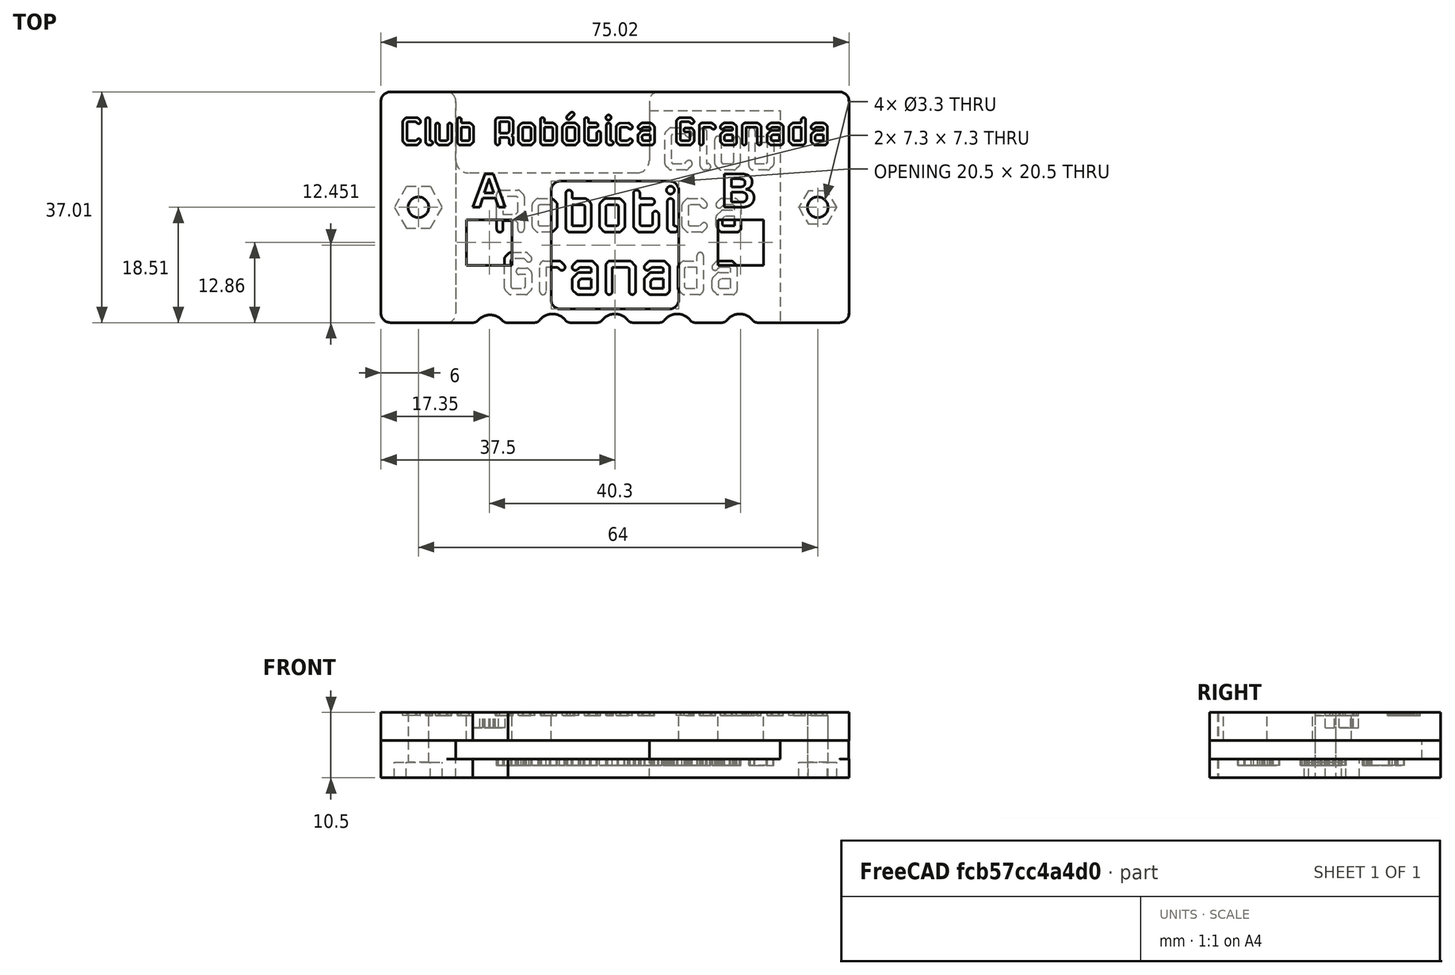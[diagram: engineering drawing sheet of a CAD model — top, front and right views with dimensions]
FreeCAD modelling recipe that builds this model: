
FCSTD DOCUMENT  (FreeCAD 0.18.4R)
Label: proteccion
License: All rights reserved
LicenseURL: http://en.wikipedia.org/wiki/All_rights_reserved
objects: Sketcher::SketchObject×8, PartDesign::Pad×8, PartDesign::Body×8, Part::Part2DObjectPython×6, Part::Extrusion×6, Part::MultiFuse×5, Part::Cut×4, Mesh::Feature×2
note: 53 computed .brp shape members not serialized (recipe doc carries the construction recipe); baked Part::Feature solids carry a one-line shape summary decoded from their .brp

FEATURE [Mesh::Feature] bas_sans_nom  label="basevv"
  Placement = pos=(0,0,0) rot=(1,0,0;1.5708rad)
FEATURE [Mesh::Feature] Haut_sans_nom  label="tapavv"
  Placement = pos=(0,0,0) rot=(1,0,0;1.5708rad)
FEATURE [Sketcher::SketchObject] Sketch
  MapMode = 5
  Support = -> [XY_Plane]
  sketch-geometry (59):
    g0: LineSegment [constr] StartX=-32.5 StartY=18.5 StartZ=0 EndX=32.5 EndY=18.5 EndZ=0
    g1: LineSegment [constr] StartX=32.5 StartY=18.5 StartZ=0 EndX=32.5 EndY=-18.5 EndZ=0
    g2: LineSegment [constr] StartX=32.5 StartY=-18.5 StartZ=0 EndX=-32.5 EndY=-18.5 EndZ=0
    g3: LineSegment [constr] StartX=-32.5 StartY=-18.5 StartZ=0 EndX=-32.5 EndY=18.5 EndZ=0
    g4: LineSegment StartX=-31 StartY=18.5 StartZ=0 EndX=-27 EndY=18.5 EndZ=0
    g5: LineSegment [constr] StartX=32.5 StartY=17 StartZ=0 EndX=32.5 EndY=-17 EndZ=0
    g6: LineSegment StartX=31 StartY=-18.5 StartZ=0 EndX=22.8496 EndY=-18.5 EndZ=0
    g7: LineSegment [constr] StartX=-32.5 StartY=-17 StartZ=0 EndX=-32.5 EndY=17 EndZ=0
    g8: ArcOfCircle [constr] CenterX=-31 CenterY=17 CenterZ=0 NormalX=0 NormalY=0 NormalZ=1 AngleXU=0 Radius=1.5 StartAngle=1.5708 EndAngle=3.14159
    g9: ArcOfCircle [constr] CenterX=-31 CenterY=-17 CenterZ=0 NormalX=0 NormalY=0 NormalZ=1 AngleXU=0 Radius=1.5 StartAngle=3.14159 EndAngle=4.71239
    g10: ArcOfCircle [constr] CenterX=31 CenterY=17 CenterZ=0 NormalX=0 NormalY=0 NormalZ=1 AngleXU=0 Radius=1.5 StartAngle=-9e-16 EndAngle=1.5708
    g11: ArcOfCircle [constr] CenterX=31 CenterY=-17 CenterZ=0 NormalX=0 NormalY=0 NormalZ=1 AngleXU=0 Radius=1.5 StartAngle=4.71239 EndAngle=6.28319
    g12: LineSegment StartX=5.5 StartY=17 StartZ=0 EndX=5.5 EndY=7.5 EndZ=0
    g13: LineSegment StartX=3.5 StartY=5.5 StartZ=0 EndX=-23.5 EndY=5.5 EndZ=0
    g14: LineSegment StartX=-25.5 StartY=7.5 StartZ=0 EndX=-25.5 EndY=17 EndZ=0
    g15: LineSegment StartX=7 StartY=18.5 StartZ=0 EndX=31 EndY=18.5 EndZ=0
    g16: ArcOfCircle CenterX=-27 CenterY=17 CenterZ=0 NormalX=0 NormalY=0 NormalZ=1 AngleXU=0 Radius=1.5 StartAngle=1e-16 EndAngle=1.5708
    g17: ArcOfCircle CenterX=7 CenterY=17 CenterZ=0 NormalX=0 NormalY=0 NormalZ=1 AngleXU=0 Radius=1.5 StartAngle=1.5708 EndAngle=3.14159
    g18: ArcOfCircle CenterX=-23.5 CenterY=7.5 CenterZ=0 NormalX=0 NormalY=0 NormalZ=1 AngleXU=0 Radius=2 StartAngle=3.14159 EndAngle=4.71239
    g19: ArcOfCircle CenterX=3.5 CenterY=7.5 CenterZ=0 NormalX=0 NormalY=0 NormalZ=1 AngleXU=0 Radius=2 StartAngle=4.71239 EndAngle=6.28319
    g20: LineSegment [constr] StartX=-20 StartY=-19.7 StartZ=0 EndX=27.6448 EndY=-19.7 EndZ=0
    g21: LineSegment [constr] StartX=-10 StartY=-19.7 StartZ=0 EndX=-10 EndY=-21.3595 EndZ=0
    g22: LineSegment [constr] StartX=-15 StartY=-19.7 StartZ=0 EndX=-15 EndY=-20.3977 EndZ=0
    g23: LineSegment [constr] StartX=-5 StartY=-19.7 StartZ=0 EndX=-5 EndY=-20.6594 EndZ=0
    g24: LineSegment [constr] StartX=0 StartY=-19.7 StartZ=0 EndX=0 EndY=-21.7167 EndZ=0
    g25: LineSegment [constr] StartX=5 StartY=-19.7 StartZ=0 EndX=5 EndY=-20.9237 EndZ=0
    g26: LineSegment [constr] StartX=10 StartY=-19.7 StartZ=0 EndX=10 EndY=-20.8482 EndZ=0
    g27: LineSegment [constr] StartX=15 StartY=-19.7 StartZ=0 EndX=15 EndY=-20.886 EndZ=0
    g28: LineSegment [constr] StartX=20 StartY=-19.7 StartZ=0 EndX=20 EndY=-21.4524 EndZ=0
    g29: ArcOfCircle CenterX=-2.84955 CenterY=-17.5 CenterZ=0 NormalX=0 NormalY=0 NormalZ=1 AngleXU=0 Radius=1 StartAngle=4.71239 EndAngle=5.62572
    g30: ArcOfCircle CenterX=0 CenterY=-19.7 CenterZ=0 NormalX=0 NormalY=0 NormalZ=1 AngleXU=0 Radius=2.6 StartAngle=0.657467 EndAngle=2.48413
    g31: ArcOfCircle CenterX=2.84955 CenterY=-17.5 CenterZ=0 NormalX=0 NormalY=0 NormalZ=1 AngleXU=0 Radius=1 StartAngle=3.79906 EndAngle=4.71232
    g32: LineSegment StartX=-2.84955 StartY=-18.5 StartZ=0 EndX=-7.15054 EndY=-18.5 EndZ=0
    g33: ArcOfCircle CenterX=7.15045 CenterY=-17.5 CenterZ=0 NormalX=0 NormalY=0 NormalZ=1 AngleXU=0 Radius=1 StartAngle=4.71239 EndAngle=5.62572
    g34: ArcOfCircle CenterX=10 CenterY=-19.7 CenterZ=0 NormalX=0 NormalY=0 NormalZ=1 AngleXU=0 Radius=2.6 StartAngle=0.657467 EndAngle=2.48413
    g35: ArcOfCircle CenterX=12.8496 CenterY=-17.5 CenterZ=0 NormalX=0 NormalY=0 NormalZ=1 AngleXU=0 Radius=1 StartAngle=3.79906 EndAngle=4.71239
    g36: LineSegment StartX=7.15045 StartY=-18.5 StartZ=0 EndX=2.84948 EndY=-18.5 EndZ=0
    g37: ArcOfCircle CenterX=17.1504 CenterY=-17.5 CenterZ=0 NormalX=0 NormalY=0 NormalZ=1 AngleXU=0 Radius=1 StartAngle=4.71239 EndAngle=5.62572
    g38: ArcOfCircle CenterX=20 CenterY=-19.7 CenterZ=0 NormalX=0 NormalY=0 NormalZ=1 AngleXU=0 Radius=2.6 StartAngle=0.657467 EndAngle=2.48413
    g39: ArcOfCircle CenterX=22.8496 CenterY=-17.5 CenterZ=0 NormalX=0 NormalY=0 NormalZ=1 AngleXU=0 Radius=1 StartAngle=3.79906 EndAngle=4.71239
    g40: LineSegment StartX=17.1504 StartY=-18.5 StartZ=0 EndX=12.8496 EndY=-18.5 EndZ=0
    g41: ArcOfCircle CenterX=-7.15046 CenterY=-17.5 CenterZ=0 NormalX=0 NormalY=0 NormalZ=1 AngleXU=0 Radius=1 StartAngle=3.79906 EndAngle=4.71232
    g42: ArcOfCircle CenterX=-10 CenterY=-19.7 CenterZ=0 NormalX=0 NormalY=0 NormalZ=1 AngleXU=0 Radius=2.6 StartAngle=0.65747 EndAngle=2.48412
    g43: ArcOfCircle CenterX=-12.8496 CenterY=-17.5 CenterZ=0 NormalX=0 NormalY=0 NormalZ=1 AngleXU=0 Radius=1 StartAngle=4.71239 EndAngle=5.62572
    g44: ArcOfCircle CenterX=-17.2845 CenterY=-17.511 CenterZ=0 NormalX=0 NormalY=0 NormalZ=1 AngleXU=0 Radius=1 StartAngle=3.8529 EndAngle=4.86087
    g45: ArcOfCircle CenterX=-20.0115 CenterY=-19.8612 CenterZ=0 NormalX=0 NormalY=0 NormalZ=1 AngleXU=0 Radius=2.6 StartAngle=0.71131 EndAngle=2.42648
    g46: ArcOfCircle CenterX=-22.7296 CenterY=-17.5006 CenterZ=0 NormalX=0 NormalY=0 NormalZ=1 AngleXU=0 Radius=1 StartAngle=4.67644 EndAngle=5.56807
    g47: LineSegment StartX=-17.1366 StartY=-18.5 StartZ=0 EndX=-12.8496 EndY=-18.5 EndZ=0
    g48: LineSegment StartX=-31 StartY=-18.5 StartZ=0 EndX=-22.7656 EndY=-18.5 EndZ=0
    g49: LineSegment StartX=-31 StartY=18.5 StartZ=0 EndX=-36 EndY=18.5 EndZ=0
    g50: LineSegment StartX=-37.5 StartY=17 StartZ=0 EndX=-37.5 EndY=-17 EndZ=0
    g51: LineSegment StartX=-36 StartY=-18.5 StartZ=0 EndX=-31 EndY=-18.5 EndZ=0
    g52: ArcOfCircle CenterX=-36 CenterY=17 CenterZ=0 NormalX=0 NormalY=0 NormalZ=1 AngleXU=0 Radius=1.5 StartAngle=1.5708 EndAngle=3.14159
    g53: ArcOfCircle CenterX=-36 CenterY=-17 CenterZ=0 NormalX=0 NormalY=0 NormalZ=1 AngleXU=0 Radius=1.5 StartAngle=3.14159 EndAngle=4.71239
    g54: LineSegment StartX=31 StartY=18.5 StartZ=0 EndX=36.0154 EndY=18.5 EndZ=0
    g55: LineSegment StartX=37.5154 StartY=17 StartZ=0 EndX=37.5154 EndY=-17 EndZ=0
    g56: LineSegment StartX=36.0154 StartY=-18.5 StartZ=0 EndX=31 EndY=-18.5 EndZ=0
    g57: ArcOfCircle CenterX=36.0154 CenterY=17 CenterZ=0 NormalX=0 NormalY=0 NormalZ=1 AngleXU=0 Radius=1.5 StartAngle=-9e-16 EndAngle=1.5708
    g58: ArcOfCircle CenterX=36.0154 CenterY=-17 CenterZ=0 NormalX=0 NormalY=0 NormalZ=1 AngleXU=0 Radius=1.5 StartAngle=4.71239 EndAngle=6.28319
  constraints (143):
    c: Coincident(g0,g1)
    c: Coincident(g1,g2)
    c: Coincident(g2,g3)
    c: Coincident(g3,g0)
    c: Horizontal(g0)
    c: Horizontal(g2)
    c: Vertical(g1)
    c: Vertical(g3)
    c: DistanceY(g1,g1) = 37
    c: Symmetric(g0,g1,g-1)
    c: Horizontal(g4)
    c: Horizontal(g6)
    c: Vertical(g5)
    c: Vertical(g7)
    c: Tangent(g4,g8) = 1.5708
    c: Tangent(g7,g8) = 1.5708
    c: Tangent(g7,g9) = 1.5708
    c: Coincident(g15,g10) = 1.5708
    c: Tangent(g5,g10) = 1.5708
    c: Tangent(g6,g11) = 1.5708
    c: Tangent(g5,g11) = 1.5708
    c: Equal(g8,g10)
    c: Equal(g10,g11)
    c: Equal(g11,g9)
    c: Radius(g8) = 1.5
    c: PointOnObject(g5,g1)
    c: PointOnObject(g15,g0)
    c: Horizontal(g13)
    c: Vertical(g12)
    c: Vertical(g14)
    c: Tangent(g4,g15)
    c: Tangent(g4,g16) = 1.5708
    c: Tangent(g14,g16) = -1.5708
    c: Tangent(g15,g17) = 1.5708
    c: Tangent(g12,g17) = -1.5708
    c: Equal(g8,g16)
    c: Equal(g16,g17)
    c: Tangent(g14,g18) = 1.5708
    c: Tangent(g13,g18) = 1.5708
    c: Tangent(g13,g19) = 1.5708
    c: Tangent(g12,g19) = 1.5708
    c: Equal(g19,g18)
    c: Radius(g18) = 2
    c: DistanceY(g13,g15) = 13
    c: DistanceX(g14,g12) = 31
    c: DistanceX(g7,g14) = 7
    c: Horizontal(g20)
    c: PointOnObject(g21,g20)
    c: Vertical(g21)
    c: PointOnObject(g22,g20)
    c: Vertical(g22)
    c: PointOnObject(g23,g20)
    c: DistanceX(g22,g21) = 5
    c: Vertical(g23)
    c: PointOnObject(g24,g20)
    c: Vertical(g24)
    c: PointOnObject(g25,g20)
    c: Vertical(g25)
    c: PointOnObject(g26,g20)
    c: Vertical(g26)
    c: PointOnObject(g27,g20)
    c: Vertical(g27)
    c: PointOnObject(g28,g20)
    c: Vertical(g28)
    c: PointOnObject(g24,g-2)
    c: DistanceX(g21,g23) = 5
    c: DistanceX(g24,g25) = 5
    c: DistanceX(g25,g26) = 5
    c: DistanceX(g26,g27) = 5
    c: DistanceX(g27,g28) = 5
    c: Tangent(g30,g31) = 1.5708
    c: Tangent(g30,g29) = 1.5708
    c: Radius(g30) = 2.6
    c: Equal(g31,g29)
    c: Radius(g31) = 1
    c: Tangent(g6,g32)
    c: Coincident(g29,g32)
    c: Coincident(g36,g31)
    c: Tangent(g34,g35) = 1.5708
    c: Tangent(g34,g33) = 1.5708
    c: Radius(g34) = 2.6
    c: Equal(g35,g33)
    c: Radius(g35) = 1
    c: Coincident(g26,g34)
    c: Coincident(g40,g35)
    c: Coincident(g36,g33)
    c: Tangent(g6,g36)
    c: Tangent(g38,g39) = 1.5708
    c: Tangent(g38,g37) = 1.5708
    c: Radius(g38) = 2.6
    c: Equal(g39,g37)
    c: Radius(g39) = 1
    c: Tangent(g6,g40)
    c: Coincident(g24,g30)
    c: Coincident(g37,g40)
    c: Coincident(g38,g28)
    c: Coincident(g39,g6)
    c: Tangent(g42,g41) = 1.5708
    c: Tangent(g42,g43) = 1.5708
    c: Radius(g42) = 2.6
    c: Equal(g41,g43)
    c: Radius(g41) = 1
    c: PointOnObject(g43,g2)
    c: Coincident(g32,g41)
    c: Tangent(g45,g44) = 1.5708
    c: Tangent(g45,g46) = 1.5708
    c: Radius(g45) = 2.6
    c: Equal(g44,g46)
    c: Radius(g44) = 1
    c: Coincident(g47,g44)
    c: Coincident(g47,g43)
    c: Horizontal(g47)
    c: Coincident(g48,g9)
    c: Coincident(g48,g46)
    c: Horizontal(g48)
    c: DistanceY(g10,g0) = 1.5
    c: PointOnObject(g9,g2)
    c: DistanceX(g7,g5) = 65
    c: Symmetric(g8,g11,g-1)
    c: Horizontal(g49)
    c: Horizontal(g51)
    c: Vertical(g50)
    c: Coincident(g49,g4)
    c: Coincident(g51,g48)
    c: DistanceX(g2,g48) = 1.5
    c: Tangent(g50,g52) = -1.5708
    c: Tangent(g49,g52) = -1.5708
    c: Equal(g52,g8)
    c: Tangent(g50,g53) = -1.5708
    c: Tangent(g51,g53) = -1.5708
    c: Equal(g9,g53)
    c: DistanceX(g50,g2) = 5
    c: Coincident(g15,g54)
    c: Horizontal(g54)
    c: Vertical(g55)
    c: Coincident(g56,g6)
    c: Horizontal(g56)
    c: Tangent(g54,g57) = 1.5708
    c: Tangent(g55,g57) = 1.5708
    c: Equal(g57,g10)
    c: Tangent(g56,g58) = 1.5708
    c: Tangent(g55,g58) = 1.5708
    c: Equal(g11,g58)
FEATURE [PartDesign::Pad] Pad
  Length = 3
  Length2 = 100
  Profile = -> Sketch
  Refine = true
  Type = 0
FEATURE [PartDesign::Body] Body  label="base"
  Group = -> [Sketch,Pad]
  Origin = -> Origin
  Tip = -> Pad
FEATURE [Part::Part2DObjectPython] ShapeString  # Draft 2D object (typed FeaturePython)
  FontFile = <path>
  Placement = pos=(8,6,2) rot=(0,0,1;0rad)
  Size = 4
  String = Club
  Tracking = 0
FEATURE [Part::Part2DObjectPython] ShapeString001  # Draft 2D object (typed FeaturePython)
  FontFile = <path>
  Placement = pos=(-18.95,-4,2) rot=(0,0,1;0rad)
  Size = 4
  String = Robotica
  Tracking = 0
FEATURE [Part::Part2DObjectPython] ShapeString002  # Draft 2D object (typed FeaturePython)
  FontFile = <path>
  Placement = pos=(-17.7,-14,2) rot=(0,0,1;0rad)
  Size = 4
  String = Granada
  Tracking = 0
FEATURE [Part::Extrusion] Extrude
  Base = -> ShapeString
  Dir = (0,0,1)
  DirMode = 2
  FaceMakerClass = Part::FaceMakerBullseye
  LengthFwd = 10
  LengthRev = 0
  Solid = true
  Symmetric = false
FEATURE [Part::Extrusion] Extrude001
  Base = -> ShapeString001
  Dir = (0,0,1)
  DirMode = 2
  FaceMakerClass = Part::FaceMakerBullseye
  LengthFwd = 10
  LengthRev = 0
  Solid = true
  Symmetric = false
FEATURE [Part::Extrusion] Extrude002
  Base = -> ShapeString002
  Dir = (0,0,1)
  DirMode = 2
  FaceMakerClass = Part::FaceMakerBullseye
  LengthFwd = 10
  LengthRev = 0
  Solid = true
  Symmetric = false
FEATURE [Part::MultiFuse] Fusion
  Refine = true
  Shapes = -> [Extrude,Extrude001,Extrude002]
FEATURE [Sketcher::SketchObject] Sketch004
  MapMode = 5
  Support = -> [XY_Plane001]
  sketch-geometry (16):
    g0: LineSegment [constr] StartX=-32.5 StartY=18.5 StartZ=0 EndX=32.5 EndY=18.5 EndZ=0
    g1: LineSegment [constr] StartX=32.5 StartY=-18.5 StartZ=0 EndX=-32.5 EndY=-18.5 EndZ=0
    g2: LineSegment [constr] StartX=-32.5 StartY=-18.5 StartZ=0 EndX=-32.5 EndY=18.5 EndZ=0
    g3: LineSegment StartX=-31 StartY=18.5 StartZ=0 EndX=-27 EndY=18.5 EndZ=0
    g4: LineSegment [constr] StartX=-32.5 StartY=-17 StartZ=0 EndX=-32.5 EndY=17 EndZ=0
    g5: ArcOfCircle [constr] CenterX=-31 CenterY=17 CenterZ=0 NormalX=0 NormalY=0 NormalZ=1 AngleXU=0 Radius=1.5 StartAngle=1.5708 EndAngle=3.14159
    g6: ArcOfCircle [constr] CenterX=-31 CenterY=-17 CenterZ=0 NormalX=0 NormalY=0 NormalZ=1 AngleXU=0 Radius=1.5 StartAngle=3.14159 EndAngle=4.71239
    g7: LineSegment StartX=-31 StartY=-18.5 StartZ=0 EndX=-27 EndY=-18.5 EndZ=0
    g8: LineSegment StartX=-31 StartY=18.5 StartZ=0 EndX=-36 EndY=18.5 EndZ=0
    g9: LineSegment StartX=-37.5 StartY=17 StartZ=0 EndX=-37.5 EndY=-17 EndZ=0
    g10: LineSegment StartX=-36 StartY=-18.5 StartZ=0 EndX=-31 EndY=-18.5 EndZ=0
    g11: ArcOfCircle CenterX=-36 CenterY=17 CenterZ=0 NormalX=0 NormalY=0 NormalZ=1 AngleXU=0 Radius=1.5 StartAngle=1.5708 EndAngle=3.14159
    g12: ArcOfCircle CenterX=-36 CenterY=-17 CenterZ=0 NormalX=0 NormalY=0 NormalZ=1 AngleXU=0 Radius=1.5 StartAngle=3.14159 EndAngle=4.71239
    g13: LineSegment StartX=-25.5 StartY=17 StartZ=0 EndX=-25.5 EndY=-17 EndZ=0
    g14: ArcOfCircle CenterX=-27 CenterY=17 CenterZ=0 NormalX=0 NormalY=0 NormalZ=1 AngleXU=0 Radius=1.5 StartAngle=8e-16 EndAngle=1.5708
    g15: ArcOfCircle CenterX=-27 CenterY=-17 CenterZ=0 NormalX=0 NormalY=0 NormalZ=1 AngleXU=0 Radius=1.5 StartAngle=4.71239 EndAngle=6.28319
  constraints (35):
    c: Coincident(g1,g2)
    c: Coincident(g2,g0)
    c: Horizontal(g0)
    c: Horizontal(g1)
    c: Vertical(g2)
    c: Horizontal(g3)
    c: Vertical(g4)
    c: Tangent(g3,g5) = 1.5708
    c: Tangent(g4,g5) = 1.5708
    c: Tangent(g4,g6) = 1.5708
    c: Radius(g5) = 1.5
    c: Coincident(g7,g6)
    c: Horizontal(g7)
    c: PointOnObject(g6,g1)
    c: Horizontal(g8)
    c: Horizontal(g10)
    c: Vertical(g9)
    c: Coincident(g8,g3)
    c: Coincident(g10,g7)
    c: DistanceX(g1,g7) = 1.5
    c: Tangent(g9,g11) = -1.5708
    c: Tangent(g8,g11) = -1.5708
    c: Equal(g11,g5)
    c: Tangent(g9,g12) = -1.5708
    c: Tangent(g10,g12) = -1.5708
    c: Equal(g6,g12)
    c: DistanceX(g9,g1) = 5
    c: Vertical(g13)
    c: Tangent(g3,g14) = 1.5708
    c: Tangent(g13,g14) = 1.5708
    c: Tangent(g7,g15) = -1.5708
    c: Tangent(g13,g15) = 1.5708
    c: Equal(g12,g15)
    c: Equal(g15,g14)
    c: DistanceX(g3,g13) = 5.5
FEATURE [Part::Cut] Cut
  Base = -> Body
  Refine = true
  Tool = -> Fusion
FEATURE [Sketcher::SketchObject] Sketch005
  MapMode = 5
  Support = -> [XY_Plane002]
  sketch-geometry (17):
    g0: LineSegment [constr] StartX=-32.5 StartY=18.5 StartZ=0 EndX=32.5 EndY=18.5 EndZ=0
    g1: LineSegment [constr] StartX=32.5 StartY=18.5 StartZ=0 EndX=32.5 EndY=-18.5 EndZ=0
    g2: LineSegment [constr] StartX=32.5 StartY=-18.5 StartZ=0 EndX=-32.5 EndY=-18.5 EndZ=0
    g3: LineSegment [constr] StartX=32.5 StartY=17 StartZ=0 EndX=32.5 EndY=-17 EndZ=0
    g4: LineSegment StartX=31 StartY=-18.5 StartZ=0 EndX=26.5 EndY=-18.5 EndZ=0
    g5: ArcOfCircle [constr] CenterX=31 CenterY=17 CenterZ=0 NormalX=0 NormalY=0 NormalZ=1 AngleXU=0 Radius=1.5 StartAngle=0 EndAngle=1.5708
    g6: ArcOfCircle [constr] CenterX=31 CenterY=-17 CenterZ=0 NormalX=0 NormalY=0 NormalZ=1 AngleXU=0 Radius=1.5 StartAngle=4.71239 EndAngle=6.28319
    g7: LineSegment StartX=7 StartY=18.5 StartZ=0 EndX=31 EndY=18.5 EndZ=0
    g8: LineSegment StartX=31 StartY=18.5 StartZ=0 EndX=35.9978 EndY=18.5 EndZ=0
    g9: LineSegment StartX=37.4978 StartY=17 StartZ=0 EndX=37.4978 EndY=-17 EndZ=0
    g10: LineSegment StartX=35.9978 StartY=-18.5 StartZ=0 EndX=31 EndY=-18.5 EndZ=0
    g11: ArcOfCircle CenterX=35.9978 CenterY=17 CenterZ=0 NormalX=0 NormalY=0 NormalZ=1 AngleXU=0 Radius=1.5 StartAngle=3e-16 EndAngle=1.5708
    g12: ArcOfCircle CenterX=35.9978 CenterY=-17 CenterZ=0 NormalX=0 NormalY=0 NormalZ=1 AngleXU=0 Radius=1.5 StartAngle=4.71239 EndAngle=6.28319
    g13: LineSegment StartX=5.5 StartY=17 StartZ=0 EndX=5.5 EndY=15.5 EndZ=0
    g14: LineSegment StartX=5.5 StartY=15.5 StartZ=0 EndX=26.5 EndY=15.5 EndZ=0
    g15: LineSegment StartX=26.5 StartY=15.5 StartZ=0 EndX=26.5 EndY=-18.5 EndZ=0
    g16: ArcOfCircle CenterX=7 CenterY=17 CenterZ=0 NormalX=0 NormalY=0 NormalZ=1 AngleXU=0 Radius=1.5 StartAngle=1.5708 EndAngle=3.14159
  constraints (39):
    c: Coincident(g0,g1)
    c: Coincident(g1,g2)
    c: Horizontal(g0)
    c: Horizontal(g2)
    c: Vertical(g1)
    c: DistanceY(g1,g1) = 37
    c: Symmetric(g0,g1,g-1)
    c: Horizontal(g4)
    c: Vertical(g3)
    c: Coincident(g7,g5) = 1.5708
    c: Tangent(g3,g5) = 1.5708
    c: Tangent(g4,g6) = 1.5708
    c: Tangent(g3,g6) = 1.5708
    c: Equal(g5,g6)
    c: PointOnObject(g3,g1)
    c: PointOnObject(g7,g0)
    c: DistanceY(g5,g0) = 1.5
    c: Coincident(g7,g8)
    c: Horizontal(g8)
    c: Vertical(g9)
    c: Coincident(g10,g4)
    c: Horizontal(g10)
    c: Tangent(g8,g11) = 1.5708
    c: Tangent(g9,g11) = 1.5708
    c: Equal(g11,g5)
    c: Tangent(g10,g12) = 1.5708
    c: Tangent(g9,g12) = 1.5708
    c: Equal(g6,g12)
    c: Vertical(g13)
    c: Coincident(g13,g14)
    c: Horizontal(g14)
    c: Coincident(g14,g15)
    c: Coincident(g15,g4)
    c: Vertical(g15)
    c: Tangent(g13,g16) = -1.5708
    c: Tangent(g7,g16) = 1.5708
    c: Equal(g16,g11)
    c: DistanceY(g13,g7) = 3
    c: DistanceX(g14,g14) = 21
FEATURE [PartDesign::Pad] Pad001
  Length = 3
  Length2 = 100
  Profile = -> Sketch004
  Refine = true
  Type = 0
FEATURE [PartDesign::Body] Body001
  Group = -> [Sketch004,Pad001]
  Origin = -> Origin001
  Placement = pos=(0,0,3) rot=(0,0,1;0rad)
  Tip = -> Pad001
FEATURE [PartDesign::Pad] Pad002
  Length = 3
  Length2 = 100
  Profile = -> Sketch005
  Refine = true
  Type = 0
FEATURE [PartDesign::Body] Body002
  Group = -> [Sketch005,Pad002]
  Origin = -> Origin002
  Placement = pos=(0,0,3) rot=(0,0,1;0rad)
  Tip = -> Pad002
FEATURE [Part::MultiFuse] Fusion001
  Refine = true
  Shapes = -> [Body002,Body001,Cut]
FEATURE [Sketcher::SketchObject] Sketch006
  MapMode = 5
  Support = -> [XY_Plane003]
  sketch-geometry (7):
    g0: LineSegment StartX=-27.6468 StartY=0 StartZ=0 EndX=-29.5734 EndY=3.33696 EndZ=0
    g1: LineSegment StartX=-29.5734 StartY=3.33696 StartZ=0 EndX=-33.4266 EndY=3.33696 EndZ=0
    g2: LineSegment StartX=-33.4266 StartY=3.33696 StartZ=0 EndX=-35.3532 EndY=0 EndZ=0
    g3: LineSegment StartX=-35.3532 StartY=0 StartZ=0 EndX=-33.4266 EndY=-3.33696 EndZ=0
    g4: LineSegment StartX=-33.4266 StartY=-3.33696 StartZ=0 EndX=-29.5734 EndY=-3.33696 EndZ=0
    g5: LineSegment StartX=-29.5734 StartY=-3.33696 StartZ=0 EndX=-27.6468 EndY=0 EndZ=0
    g6: Circle [constr] CenterX=-31.5 CenterY=0 CenterZ=0 NormalX=0 NormalY=0 NormalZ=1 AngleXU=0 Radius=3.85319
  constraints (16):
    c: Coincident(g0,g1)
    c: Coincident(g1,g2)
    c: Coincident(g2,g3)
    c: Coincident(g3,g4)
    c: Coincident(g4,g5)
    c: Coincident(g5,g0)
    c: Equal(g0, g1-g5) x5
    c: PointOnObject(g0,g6)
    c: PointOnObject(g1,g6)
    c: PointOnObject(g2,g6)
    c: PointOnObject(g3,g6)
    c: PointOnObject(g4,g6)
    c: PointOnObject(g5,g6)
    c: PointOnObject(g6,g-1)
    c: PointOnObject(g5,g-1)
    c: DistanceX(g6,g-1) = 31.5
FEATURE [Sketcher::SketchObject] Sketch007
  MapMode = 5
  Support = -> [XY_Plane004]
  sketch-geometry (8):
    g0: LineSegment StartX=35.55 StartY=0 StartZ=0 EndX=34.025 EndY=2.64138 EndZ=0
    g1: LineSegment StartX=34.025 StartY=2.64138 StartZ=0 EndX=30.975 EndY=2.64138 EndZ=0
    g2: LineSegment StartX=30.975 StartY=2.64138 StartZ=0 EndX=29.45 EndY=0 EndZ=0
    g3: LineSegment StartX=29.45 StartY=0 StartZ=0 EndX=30.975 EndY=-2.64138 EndZ=0
    g4: LineSegment StartX=30.975 StartY=-2.64138 StartZ=0 EndX=34.025 EndY=-2.64138 EndZ=0
    g5: LineSegment StartX=34.025 StartY=-2.64138 StartZ=0 EndX=35.55 EndY=0 EndZ=0
    g6: Circle [constr] CenterX=32.5 CenterY=3.704e-13 CenterZ=0 NormalX=0 NormalY=0 NormalZ=1 AngleXU=0 Radius=3.05
    g7: LineSegment [constr] StartX=32.5 StartY=3.704e-13 StartZ=0 EndX=32.5 EndY=5.42446 EndZ=0
  constraints (19):
    c: Coincident(g0,g1)
    c: Coincident(g1,g2)
    c: Coincident(g2,g3)
    c: Coincident(g3,g4)
    c: Coincident(g4,g5)
    c: Coincident(g5,g0)
    c: Equal(g0, g1-g5) x5
    c: PointOnObject(g0,g6)
    c: PointOnObject(g1,g6)
    c: PointOnObject(g2,g6)
    c: PointOnObject(g3,g6)
    c: PointOnObject(g4,g6)
    c: PointOnObject(g5,g6)
    c: PointOnObject(g5,g-1)
    c: Diameter(g6) = 6.1
    c: PointOnObject(g2,g-1)
    c: Vertical(g7)
    c: DistanceX(g-1,g7) = 32.5
    c: Coincident(g6,g7)
FEATURE [PartDesign::Pad] Pad003
  Length = 2.5
  Length2 = 100
  Profile = -> Sketch006
  Refine = true
  Type = 0
FEATURE [PartDesign::Body] Body003
  Group = -> [Sketch006,Pad003]
  Origin = -> Origin003
  Tip = -> Pad003
FEATURE [PartDesign::Pad] Pad004
  Length = 2.5
  Length2 = 100
  Profile = -> Sketch007
  Refine = true
  Type = 0
FEATURE [PartDesign::Body] Body004
  Group = -> [Sketch007,Pad004]
  Origin = -> Origin004
  Tip = -> Pad004
FEATURE [Part::MultiFuse] Fusion002
  Refine = true
  Shapes = -> [Pad003,Pad004]
FEATURE [Part::Cut] Cut001
  Base = -> Fusion001
  Refine = true
  Tool = -> Fusion002
FEATURE [Sketcher::SketchObject] Sketch008
  MapMode = 5
  Support = -> [XY_Plane005]
  sketch-geometry (1):
    g0: Circle CenterX=-31.5 CenterY=0 CenterZ=0 NormalX=0 NormalY=0 NormalZ=1 AngleXU=0 Radius=1.65
  constraints (3):
    c: PointOnObject(g0,g-1)
    c: Diameter(g0) = 3.3
    c: DistanceX(g0,g-1) = 31.5
FEATURE [PartDesign::Pad] Pad005
  Length = 10
  Length2 = 100
  Profile = -> Sketch008
  Refine = true
  Type = 0
FEATURE [PartDesign::Body] Body005
  Group = -> [Sketch008,Pad005]
  Origin = -> Origin005
  Tip = -> Pad005
FEATURE [Sketcher::SketchObject] Sketch009
  MapMode = 5
  Support = -> [XY_Plane006]
  sketch-geometry (1):
    g0: Circle CenterX=32.5 CenterY=0 CenterZ=0 NormalX=0 NormalY=0 NormalZ=1 AngleXU=0 Radius=1.65
  constraints (3):
    c: PointOnObject(g0,g-1)
    c: Diameter(g0) = 3.3
    c: DistanceX(g-1,g0) = 32.5
FEATURE [PartDesign::Pad] Pad006
  Length = 10
  Length2 = 100
  Profile = -> Sketch009
  Refine = true
  Type = 0
FEATURE [PartDesign::Body] Body006
  Group = -> [Sketch009,Pad006]
  Origin = -> Origin006
  Tip = -> Pad006
FEATURE [Part::MultiFuse] Fusion003
  Refine = true
  Shapes = -> [Body005,Pad006]
FEATURE [Part::Cut] Cut002  label="base-final"
  Base = -> Cut001
  Refine = true
  Tool = -> Fusion003
FEATURE [Sketcher::SketchObject] Sketch010
  MapMode = 5
  Support = -> [XY_Plane007]
  sketch-geometry (71):
    g0: LineSegment [constr] StartX=-32.5 StartY=18.5 StartZ=0 EndX=32.5 EndY=18.5 EndZ=0
    g1: LineSegment [constr] StartX=32.5 StartY=18.5 StartZ=0 EndX=32.5 EndY=-18.5 EndZ=0
    g2: LineSegment [constr] StartX=32.5 StartY=-18.5 StartZ=0 EndX=-32.5 EndY=-18.5 EndZ=0
    g3: LineSegment [constr] StartX=-32.5 StartY=-18.5 StartZ=0 EndX=-32.5 EndY=18.5 EndZ=0
    g4: LineSegment StartX=-31 StartY=18.5 StartZ=0 EndX=-27 EndY=18.5 EndZ=0
    g5: LineSegment [constr] StartX=32.5 StartY=17 StartZ=0 EndX=32.5 EndY=-17 EndZ=0
    g6: LineSegment StartX=31 StartY=-18.5 StartZ=0 EndX=22.8496 EndY=-18.5 EndZ=0
    g7: LineSegment [constr] StartX=-32.5 StartY=-17 StartZ=0 EndX=-32.5 EndY=17 EndZ=0
    g8: ArcOfCircle [constr] CenterX=-31 CenterY=17 CenterZ=0 NormalX=0 NormalY=0 NormalZ=1 AngleXU=0 Radius=1.5 StartAngle=1.5708 EndAngle=3.14159
    g9: ArcOfCircle [constr] CenterX=-31 CenterY=-17 CenterZ=0 NormalX=0 NormalY=0 NormalZ=1 AngleXU=0 Radius=1.5 StartAngle=3.14159 EndAngle=4.71239
    g10: ArcOfCircle [constr] CenterX=31 CenterY=17 CenterZ=0 NormalX=0 NormalY=0 NormalZ=1 AngleXU=0 Radius=1.5 StartAngle=-9e-16 EndAngle=1.5708
    g11: ArcOfCircle [constr] CenterX=31 CenterY=-17 CenterZ=0 NormalX=0 NormalY=0 NormalZ=1 AngleXU=0 Radius=1.5 StartAngle=4.71239 EndAngle=6.28319
    g12: LineSegment StartX=7 StartY=18.5 StartZ=0 EndX=31 EndY=18.5 EndZ=0
    g13: LineSegment [constr] StartX=-20 StartY=-19.7 StartZ=0 EndX=27.6448 EndY=-19.7 EndZ=0
    g14: LineSegment [constr] StartX=-10 StartY=-19.7 StartZ=0 EndX=-10 EndY=-21.3595 EndZ=0
    g15: LineSegment [constr] StartX=-15 StartY=-19.7 StartZ=0 EndX=-15 EndY=-20.3977 EndZ=0
    g16: LineSegment [constr] StartX=-5 StartY=-19.7 StartZ=0 EndX=-5 EndY=-20.6594 EndZ=0
    g17: LineSegment [constr] StartX=0 StartY=-19.7 StartZ=0 EndX=0 EndY=-21.7167 EndZ=0
    g18: LineSegment [constr] StartX=5 StartY=-19.7 StartZ=0 EndX=5 EndY=-20.9237 EndZ=0
    g19: LineSegment [constr] StartX=10 StartY=-19.7 StartZ=0 EndX=10 EndY=-20.8482 EndZ=0
    g20: LineSegment [constr] StartX=15 StartY=-19.7 StartZ=0 EndX=15 EndY=-20.886 EndZ=0
    g21: LineSegment [constr] StartX=20 StartY=-19.7 StartZ=0 EndX=20 EndY=-21.4524 EndZ=0
    g22: ArcOfCircle CenterX=-2.84955 CenterY=-17.5 CenterZ=0 NormalX=0 NormalY=0 NormalZ=1 AngleXU=0 Radius=1 StartAngle=4.71239 EndAngle=5.62572
    g23: ArcOfCircle CenterX=0 CenterY=-19.7 CenterZ=0 NormalX=0 NormalY=0 NormalZ=1 AngleXU=0 Radius=2.6 StartAngle=0.657467 EndAngle=2.48413
    g24: ArcOfCircle CenterX=2.84955 CenterY=-17.5 CenterZ=0 NormalX=0 NormalY=0 NormalZ=1 AngleXU=0 Radius=1 StartAngle=3.79906 EndAngle=4.71232
    g25: LineSegment StartX=-2.84955 StartY=-18.5 StartZ=0 EndX=-7.15054 EndY=-18.5 EndZ=0
    g26: ArcOfCircle CenterX=7.15045 CenterY=-17.5 CenterZ=0 NormalX=0 NormalY=0 NormalZ=1 AngleXU=0 Radius=1 StartAngle=4.71239 EndAngle=5.62572
    g27: ArcOfCircle CenterX=10 CenterY=-19.7 CenterZ=0 NormalX=0 NormalY=0 NormalZ=1 AngleXU=0 Radius=2.6 StartAngle=0.657467 EndAngle=2.48413
    g28: ArcOfCircle CenterX=12.8496 CenterY=-17.5 CenterZ=0 NormalX=0 NormalY=0 NormalZ=1 AngleXU=0 Radius=1 StartAngle=3.79906 EndAngle=4.71239
    g29: LineSegment StartX=7.15045 StartY=-18.5 StartZ=0 EndX=2.84948 EndY=-18.5 EndZ=0
    g30: ArcOfCircle CenterX=17.1504 CenterY=-17.5 CenterZ=0 NormalX=0 NormalY=0 NormalZ=1 AngleXU=0 Radius=1 StartAngle=4.71239 EndAngle=5.62572
    g31: ArcOfCircle CenterX=20 CenterY=-19.7 CenterZ=0 NormalX=0 NormalY=0 NormalZ=1 AngleXU=0 Radius=2.6 StartAngle=0.657467 EndAngle=2.48413
    g32: ArcOfCircle CenterX=22.8496 CenterY=-17.5 CenterZ=0 NormalX=0 NormalY=0 NormalZ=1 AngleXU=0 Radius=1 StartAngle=3.79906 EndAngle=4.71239
    g33: LineSegment StartX=17.1504 StartY=-18.5 StartZ=0 EndX=12.8496 EndY=-18.5 EndZ=0
    g34: ArcOfCircle CenterX=-7.15046 CenterY=-17.5 CenterZ=0 NormalX=0 NormalY=0 NormalZ=1 AngleXU=0 Radius=1 StartAngle=3.79906 EndAngle=4.71232
    g35: ArcOfCircle CenterX=-10 CenterY=-19.7 CenterZ=0 NormalX=0 NormalY=0 NormalZ=1 AngleXU=0 Radius=2.6 StartAngle=0.65747 EndAngle=2.48412
    g36: ArcOfCircle CenterX=-12.8496 CenterY=-17.5 CenterZ=0 NormalX=0 NormalY=0 NormalZ=1 AngleXU=0 Radius=1 StartAngle=4.71239 EndAngle=5.62572
    g37: ArcOfCircle CenterX=-17.2845 CenterY=-17.511 CenterZ=0 NormalX=0 NormalY=0 NormalZ=1 AngleXU=0 Radius=1 StartAngle=3.8529 EndAngle=4.86087
    g38: ArcOfCircle CenterX=-20.0115 CenterY=-19.8612 CenterZ=0 NormalX=0 NormalY=0 NormalZ=1 AngleXU=0 Radius=2.6 StartAngle=0.71131 EndAngle=2.42648
    g39: ArcOfCircle CenterX=-22.7296 CenterY=-17.5006 CenterZ=0 NormalX=0 NormalY=0 NormalZ=1 AngleXU=0 Radius=1 StartAngle=4.67644 EndAngle=5.56807
    g40: LineSegment StartX=-17.1366 StartY=-18.5 StartZ=0 EndX=-12.8496 EndY=-18.5 EndZ=0
    g41: LineSegment StartX=-31 StartY=-18.5 StartZ=0 EndX=-22.7656 EndY=-18.5 EndZ=0
    g42: LineSegment StartX=-31 StartY=18.5 StartZ=0 EndX=-36 EndY=18.5 EndZ=0
    g43: LineSegment StartX=-37.5 StartY=17 StartZ=0 EndX=-37.5 EndY=-17 EndZ=0
    g44: LineSegment StartX=-36 StartY=-18.5 StartZ=0 EndX=-31 EndY=-18.5 EndZ=0
    g45: ArcOfCircle CenterX=-36 CenterY=17 CenterZ=0 NormalX=0 NormalY=0 NormalZ=1 AngleXU=0 Radius=1.5 StartAngle=1.5708 EndAngle=3.14159
    g46: ArcOfCircle CenterX=-36 CenterY=-17 CenterZ=0 NormalX=0 NormalY=0 NormalZ=1 AngleXU=0 Radius=1.5 StartAngle=3.14159 EndAngle=4.71239
    g47: LineSegment StartX=31 StartY=18.5 StartZ=0 EndX=36.0116 EndY=18.5 EndZ=0
    g48: LineSegment StartX=37.5116 StartY=17 StartZ=0 EndX=37.5116 EndY=-17 EndZ=0
    g49: LineSegment StartX=36.0116 StartY=-18.5 StartZ=0 EndX=31 EndY=-18.5 EndZ=0
    g50: ArcOfCircle CenterX=36.0116 CenterY=17 CenterZ=0 NormalX=0 NormalY=0 NormalZ=1 AngleXU=0 Radius=1.5 StartAngle=1e-16 EndAngle=1.5708
    g51: ArcOfCircle CenterX=36.0116 CenterY=-17 CenterZ=0 NormalX=0 NormalY=0 NormalZ=1 AngleXU=0 Radius=1.5 StartAngle=4.71239 EndAngle=6.28319
    g52: LineSegment StartX=-27 StartY=18.5 StartZ=0 EndX=7 EndY=18.5 EndZ=0
    g53: LineSegment StartX=-23.8 StartY=-2 StartZ=0 EndX=-16.5 EndY=-2 EndZ=0
    g54: LineSegment StartX=-16.5 StartY=-2 StartZ=0 EndX=-16.5 EndY=-9.3 EndZ=0
    g55: LineSegment StartX=-16.5 StartY=-9.3 StartZ=0 EndX=-23.8 EndY=-9.3 EndZ=0
    g56: LineSegment StartX=-23.8 StartY=-9.3 StartZ=0 EndX=-23.8 EndY=-2 EndZ=0
    g57: LineSegment StartX=16.5 StartY=-2 StartZ=0 EndX=23.8 EndY=-2 EndZ=0
    g58: LineSegment StartX=23.8 StartY=-2 StartZ=0 EndX=23.8 EndY=-9.3 EndZ=0
    g59: LineSegment StartX=23.8 StartY=-9.3 StartZ=0 EndX=16.5 EndY=-9.3 EndZ=0
    g60: LineSegment StartX=16.5 StartY=-9.3 StartZ=0 EndX=16.5 EndY=-2 EndZ=0
    g61: Circle CenterX=-31.5 CenterY=0 CenterZ=0 NormalX=0 NormalY=0 NormalZ=1 AngleXU=0 Radius=1.65
    g62: Circle CenterX=32.5 CenterY=0 CenterZ=0 NormalX=0 NormalY=0 NormalZ=1 AngleXU=0 Radius=1.65
    g63: LineSegment StartX=-8.75 StartY=4.19082 StartZ=0 EndX=8.75 EndY=4.19082 EndZ=0
    g64: LineSegment StartX=10.25 StartY=2.69082 StartZ=0 EndX=10.25 EndY=-14.8092 EndZ=0
    g65: LineSegment StartX=8.75 StartY=-16.3092 StartZ=0 EndX=-8.75 EndY=-16.3092 EndZ=0
    g66: LineSegment StartX=-10.25 StartY=-14.8092 StartZ=0 EndX=-10.25 EndY=2.69082 EndZ=0
    g67: ArcOfCircle CenterX=-8.75 CenterY=2.69082 CenterZ=0 NormalX=0 NormalY=0 NormalZ=1 AngleXU=0 Radius=1.5 StartAngle=1.5708 EndAngle=3.14159
    g68: ArcOfCircle CenterX=8.75 CenterY=2.69082 CenterZ=0 NormalX=0 NormalY=0 NormalZ=1 AngleXU=0 Radius=1.5 StartAngle=0 EndAngle=1.5708
    g69: ArcOfCircle CenterX=8.75 CenterY=-14.8092 CenterZ=0 NormalX=0 NormalY=0 NormalZ=1 AngleXU=0 Radius=1.5 StartAngle=4.71239 EndAngle=6.28319
    g70: ArcOfCircle CenterX=-8.75 CenterY=-14.8092 CenterZ=0 NormalX=0 NormalY=0 NormalZ=1 AngleXU=0 Radius=1.5 StartAngle=3.14159 EndAngle=4.71239
  constraints (175):
    c: Coincident(g0,g1)
    c: Coincident(g1,g2)
    c: Coincident(g2,g3)
    c: Coincident(g3,g0)
    c: Horizontal(g0)
    c: Horizontal(g2)
    c: Vertical(g1)
    c: Vertical(g3)
    c: DistanceY(g1,g1) = 37
    c: Symmetric(g0,g1,g-1)
    c: Horizontal(g4)
    c: Horizontal(g6)
    c: Vertical(g5)
    c: Vertical(g7)
    c: Tangent(g4,g8) = 1.5708
    c: Tangent(g7,g8) = 1.5708
    c: Tangent(g7,g9) = 1.5708
    c: Coincident(g12,g10) = 1.5708
    c: Tangent(g5,g10) = 1.5708
    c: Tangent(g6,g11) = 1.5708
    c: Tangent(g5,g11) = 1.5708
    c: Equal(g8,g10)
    c: Equal(g10,g11)
    c: Equal(g11,g9)
    c: Radius(g8) = 1.5
    c: PointOnObject(g5,g1)
    c: PointOnObject(g12,g0)
    c: Tangent(g4,g12)
    c: Horizontal(g13)
    c: PointOnObject(g14,g13)
    c: Vertical(g14)
    c: PointOnObject(g15,g13)
    c: Vertical(g15)
    c: PointOnObject(g16,g13)
    c: DistanceX(g15,g14) = 5
    c: Vertical(g16)
    c: PointOnObject(g17,g13)
    c: Vertical(g17)
    c: PointOnObject(g18,g13)
    c: Vertical(g18)
    c: PointOnObject(g19,g13)
    c: Vertical(g19)
    c: PointOnObject(g20,g13)
    c: Vertical(g20)
    c: PointOnObject(g21,g13)
    c: Vertical(g21)
    c: PointOnObject(g17,g-2)
    c: DistanceX(g14,g16) = 5
    c: DistanceX(g17,g18) = 5
    c: DistanceX(g18,g19) = 5
    c: DistanceX(g19,g20) = 5
    c: DistanceX(g20,g21) = 5
    c: Tangent(g23,g24) = 1.5708
    c: Tangent(g23,g22) = 1.5708
    c: Radius(g23) = 2.6
    c: Equal(g24,g22)
    c: Radius(g24) = 1
    c: Tangent(g6,g25)
    c: Coincident(g22,g25)
    c: Coincident(g29,g24)
    c: Tangent(g27,g28) = 1.5708
    c: Tangent(g27,g26) = 1.5708
    c: Radius(g27) = 2.6
    c: Equal(g28,g26)
    c: Radius(g28) = 1
    c: Coincident(g19,g27)
    c: Coincident(g33,g28)
    c: Coincident(g29,g26)
    c: Tangent(g6,g29)
    c: Tangent(g31,g32) = 1.5708
    c: Tangent(g31,g30) = 1.5708
    c: Radius(g31) = 2.6
    c: Equal(g32,g30)
    c: Radius(g32) = 1
    c: Tangent(g6,g33)
    c: Coincident(g17,g23)
    c: Coincident(g30,g33)
    c: Coincident(g31,g21)
    c: Coincident(g32,g6)
    c: Tangent(g35,g34) = 1.5708
    c: Tangent(g35,g36) = 1.5708
    c: Radius(g35) = 2.6
    c: Equal(g34,g36)
    c: Radius(g34) = 1
    c: PointOnObject(g36,g2)
    c: Coincident(g25,g34)
    c: Tangent(g38,g37) = 1.5708
    c: Tangent(g38,g39) = 1.5708
    c: Radius(g38) = 2.6
    c: Equal(g37,g39)
    c: Radius(g37) = 1
    c: Coincident(g40,g37)
    c: Coincident(g40,g36)
    c: Horizontal(g40)
    c: Coincident(g41,g9)
    c: Coincident(g41,g39)
    c: Horizontal(g41)
    c: DistanceY(g10,g0) = 1.5
    c: PointOnObject(g9,g2)
    c: DistanceX(g7,g5) = 65
    c: Symmetric(g8,g11,g-1)
    c: Horizontal(g42)
    c: Horizontal(g44)
    c: Vertical(g43)
    c: Coincident(g42,g4)
    c: Coincident(g44,g41)
    c: DistanceX(g2,g41) = 1.5
    c: Tangent(g43,g45) = -1.5708
    c: Tangent(g42,g45) = -1.5708
    c: Equal(g45,g8)
    c: Tangent(g43,g46) = -1.5708
    c: Tangent(g44,g46) = -1.5708
    c: Equal(g9,g46)
    c: DistanceX(g43,g2) = 5
    c: Coincident(g12,g47)
    c: Horizontal(g47)
    c: Vertical(g48)
    c: Coincident(g49,g6)
    c: Horizontal(g49)
    c: Tangent(g47,g50) = 1.5708
    c: Tangent(g48,g50) = 1.5708
    c: Equal(g50,g10)
    c: Tangent(g49,g51) = 1.5708
    c: Tangent(g48,g51) = 1.5708
    c: Equal(g11,g51)
    c: Coincident(g52,g4)
    c: Coincident(g52,g12)
    c: Coincident(g53,g54)
    c: Coincident(g54,g55)
    c: Coincident(g55,g56)
    c: Coincident(g56,g53)
    c: Horizontal(g53)
    c: Horizontal(g55)
    c: Vertical(g54)
    c: Vertical(g56)
    c: Coincident(g57,g58)
    c: Coincident(g58,g59)
    c: Coincident(g59,g60)
    c: Coincident(g60,g57)
    c: Horizontal(g57)
    c: Horizontal(g59)
    c: Vertical(g58)
    c: Vertical(g60)
    c: Equal(g57,g53)
    c: Equal(g54,g58)
    c: DistanceX(g53,g-1) = 16.5
    c: DistanceX(g-1,g57) = 16.5
    c: DistanceY(g53,g-1) = 2
    c: DistanceY(g57,g-1) = 2
    c: DistanceX(g53,g53) = 7.3
    c: DistanceY(g54,g54) = 7.3
    c: PointOnObject(g61,g-1)
    c: PointOnObject(g62,g-1)
    c: Horizontal(g63)
    c: Horizontal(g65)
    c: Vertical(g64)
    c: Vertical(g66)
    c: Tangent(g66,g67) = 1.5708
    c: Tangent(g63,g67) = 1.5708
    c: Tangent(g63,g68) = 1.5708
    c: Tangent(g64,g68) = 1.5708
    c: Tangent(g65,g69) = 1.5708
    c: Tangent(g64,g69) = 1.5708
    c: Tangent(g65,g70) = 1.5708
    c: Tangent(g66,g70) = 1.5708
    c: Equal(g70,g69)
    c: Equal(g69,g68)
    c: Radius(g67) = 1.5
    c: DistanceX(g66,g64) = 20.5
    c: DistanceY(g65,g63) = 20.5
    c: Equal(g61,g62)
    c: Diameter(g61) = 3.3
    c: DistanceX(g61,g-1) = 31.5
    c: DistanceX(g-1,g62) = 32.5
    c: Symmetric(g66,g64,g-2)
FEATURE [PartDesign::Pad] Pad007
  Length = 4.5
  Length2 = 100
  Profile = -> Sketch010
  Refine = true
  Type = 0
FEATURE [PartDesign::Body] Body007
  Group = -> [Sketch010,Pad007]
  Origin = -> Origin007
  Tip = -> Pad007
FEATURE [Part::Part2DObjectPython] ShapeString003  # Draft 2D object (typed FeaturePython)
  FontFile = <path>
  Placement = pos=(-23,0,2) rot=(0,0,1;0rad)
  Size = 6
  String = A
  Tracking = 0
FEATURE [Part::Part2DObjectPython] ShapeString004  # Draft 2D object (typed FeaturePython)
  FontFile = <path>
  Placement = pos=(17,0,4) rot=(0,0,1;0rad)
  Size = 6
  String = B
  Tracking = 0
FEATURE [Part::Part2DObjectPython] ShapeString005  # Draft 2D object (typed FeaturePython)
  FontFile = <path>
  Placement = pos=(-34,10,4) rot=(0,0,1;0rad)
  Size = 2.6
  String = Club Robótica Granada
  Tracking = 0
FEATURE [Part::Extrusion] Extrude003
  Base = -> ShapeString003
  Dir = (0,0,1)
  DirMode = 2
  FaceMakerClass = Part::FaceMakerBullseye
  LengthFwd = 10
  LengthRev = 0
  Solid = true
  Symmetric = false
FEATURE [Part::Extrusion] Extrude004
  Base = -> ShapeString004
  Dir = (0,0,1)
  DirMode = 2
  FaceMakerClass = Part::FaceMakerBullseye
  LengthFwd = 10
  LengthRev = 0
  Solid = true
  Symmetric = false
FEATURE [Part::Extrusion] Extrude005
  Base = -> ShapeString005
  Dir = (0,0,1)
  DirMode = 2
  FaceMakerClass = Part::FaceMakerBullseye
  LengthFwd = 10
  LengthRev = 0
  Solid = true
  Symmetric = false
FEATURE [Part::MultiFuse] Fusion004
  Refine = true
  Shapes = -> [Extrude003,Extrude004,Extrude005]
FEATURE [Part::Cut] Cut003  label="tapa-final"
  Base = -> Body007
  Placement = pos=(0,0,6) rot=(0,0,1;0rad)
  Refine = true
  Tool = -> Fusion004
note: 6 file-system paths scrubbed to <path> (originals preserved in the JSON sidecar)
